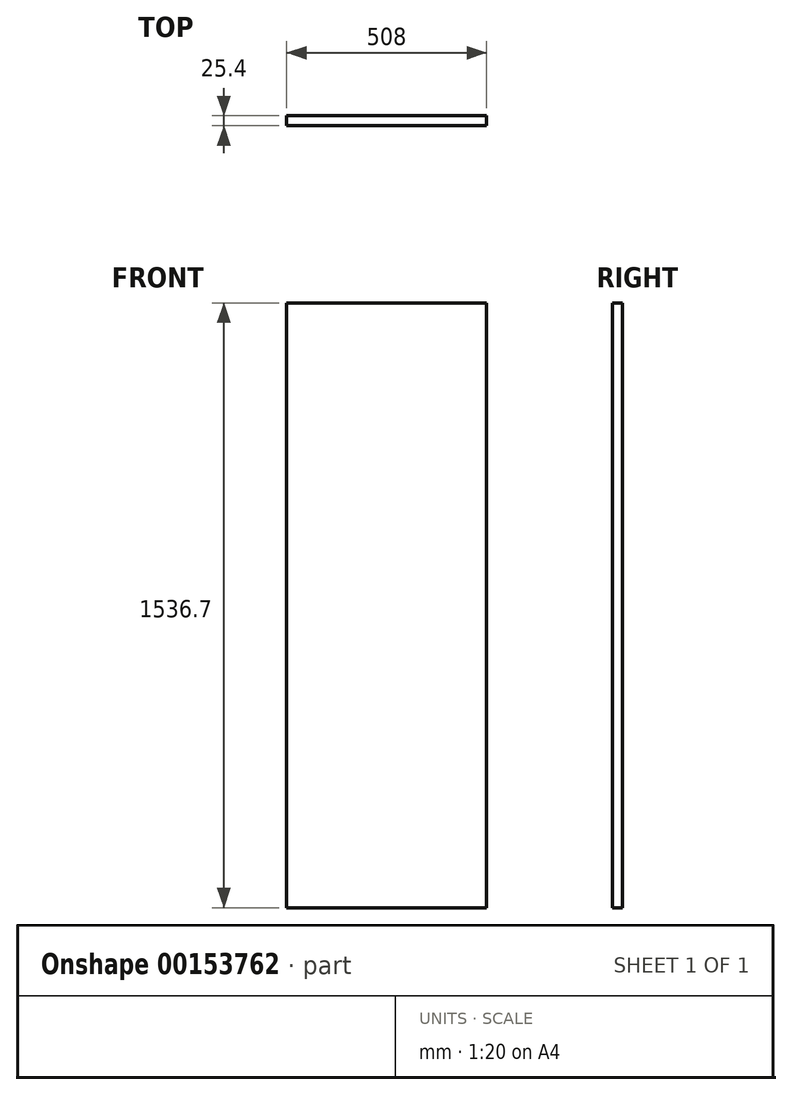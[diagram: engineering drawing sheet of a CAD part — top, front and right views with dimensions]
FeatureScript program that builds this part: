
annotation { "Feature Type Name" : "Feature", "Feature Type Description" : "" }
export const myFeature = defineFeature(function(context is Context, id is Id, definition is map)
    precondition{}
    {
        {
            var Q0;
            Q0=qCreatedBy(makeId("Front.planeOp"),FACE);
            var sketch = newSketch(context, id + "F0", { "sketchPlane" : qUnion([Q0])});
            skLineSegment(sketch, "E0.bottom", {"start": v(254, 768.35) * mm, "end": v(-254, 768.35) * mm});
            skLineSegment(sketch, "E0.top", {"start": v(254, -768.35) * mm, "end": v(-254, -768.35) * mm});
            skLineSegment(sketch, "E0.left", {"start": v(254, 768.35) * mm, "end": v(254, -768.35) * mm});
            skLineSegment(sketch, "E0.right", {"start": v(-254, 768.35) * mm, "end": v(-254, -768.35) * mm});
            skPoint(sketch, "E0.middle", {"position": v(0, 0) * mm});
            skSolve(sketch);
        }
        {
            var Q0;
            Q0 = qSketchRegion(id + "F0", true);
            extrude(context, id + "F1", {"entities" : qUnion([Q0]), "depth" : 25.4 * mm});
        }
    });
